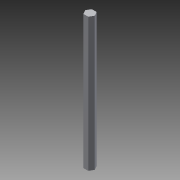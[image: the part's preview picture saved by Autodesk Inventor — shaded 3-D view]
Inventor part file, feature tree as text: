
AUTODESK INVENTOR PART (.ipt)
format: ipt  version: 2013 (Build 170138000, 138)  size: 69,632 bytes
history: native  units: in
note: dims shown in document units (in); Inventor stores cm internally (conversion verified against a paired STEP export)
features: extrude x1, sketch x1
ambient origin geometry x8: Origin, YZ Plane, XZ Plane, XY Plane, X Axis, Y Axis, Z Axis, Center Point
bodies: Solid1 (feature_tree)
feature tree (2):
  extrude  "Extrusion1"  Depth=0.375in
  sketch  "Sketch1"  dims[d1=6.0in d2=0.0in d3=0.375in]
